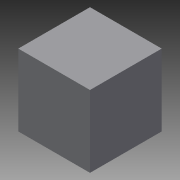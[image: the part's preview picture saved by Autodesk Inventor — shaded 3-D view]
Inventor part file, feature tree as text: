
AUTODESK INVENTOR PART (.ipt)
format: ipt  version: 2014 (Build 180170000, 170)  size: 67,584 bytes
history: native  units: in
note: dims shown in document units (in); Inventor stores cm internally (conversion verified against a paired STEP export)
features: extrude x1, sketch x1
ambient origin geometry x8: Origin, YZ Plane, XZ Plane, XY Plane, X Axis, Y Axis, Z Axis, Center Point
bodies: Solid1 (feature_tree)
feature tree (2):
  extrude  "Extrusion1"  Depth=1.0in
  sketch  "Sketch1"  dims[d0=1.0in d1=1.0in d2=1.0in d3=0.0in]
